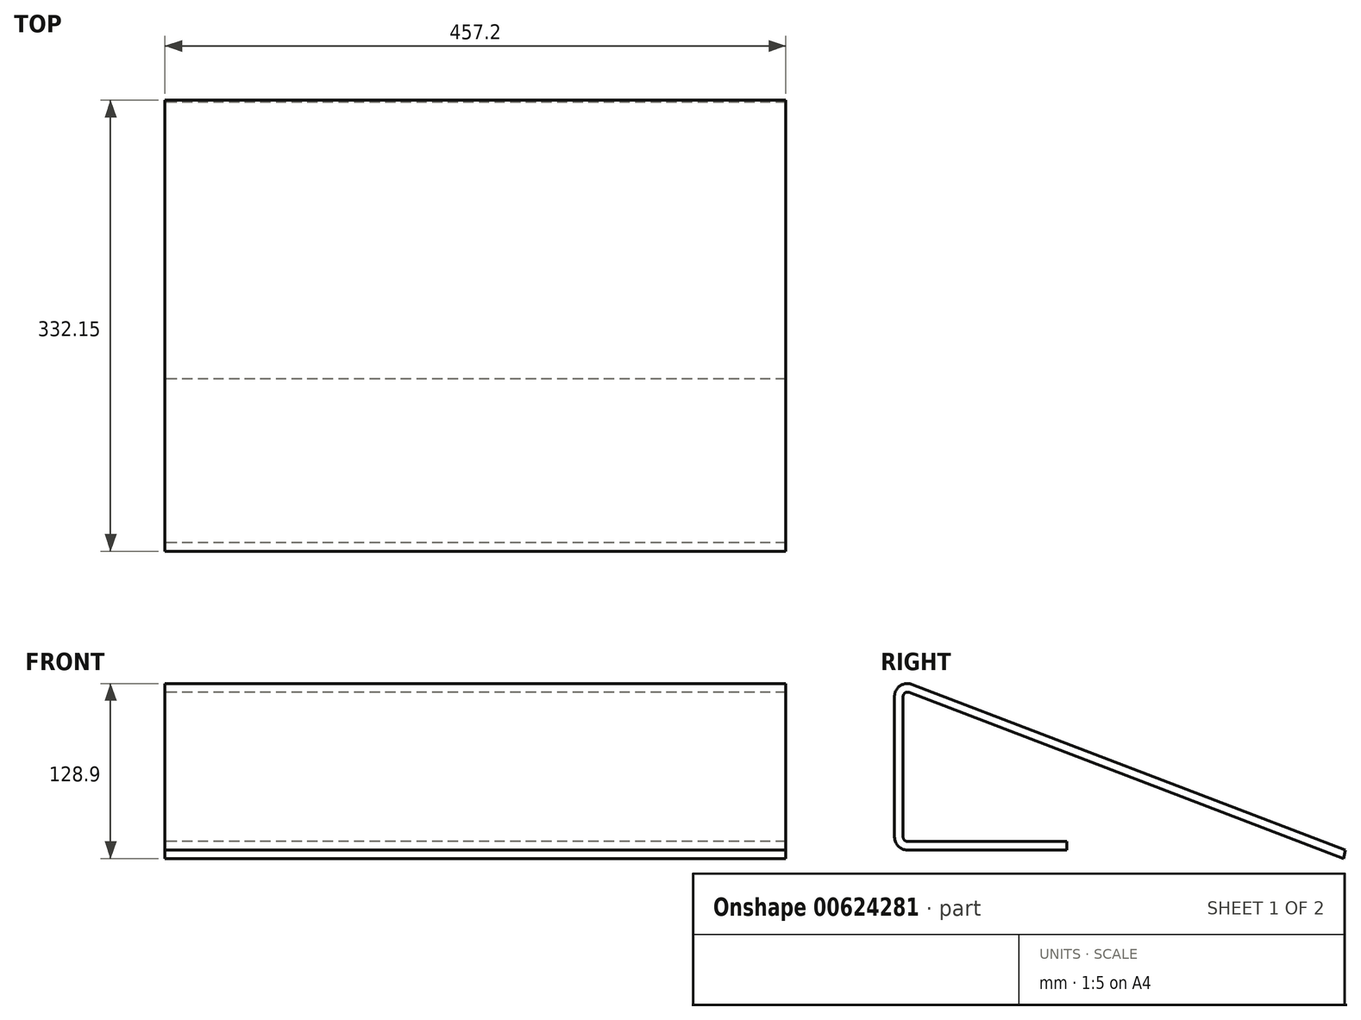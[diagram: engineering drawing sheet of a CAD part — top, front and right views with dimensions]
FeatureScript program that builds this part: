
annotation { "Feature Type Name" : "Feature", "Feature Type Description" : "" }
export const myFeature = defineFeature(function(context is Context, id is Id, definition is map)
    precondition{}
    {
        {
            var Q0;
            Q0=qCreatedBy(makeId("Right.planeOp"),FACE);
            var sketch = newSketch(context, id + "F0", { "sketchPlane" : qUnion([Q0])});
            skLineSegment(sketch, "E0", {"start": v(0, 0) * mm, "end": v(-117.47, 0) * mm});
            skLineSegment(sketch, "E1", {"start": v(-127, 9.52) * mm, "end": v(-127, 113.16) * mm});
            skLineSegment(sketch, "E2", {"start": v(-114.07, 122.06) * mm, "end": v(205.15, 0) * mm});
            skPoint(sketch, "E3.visualSharp", {"position": v(-127, 127) * mm});
            skArc(sketch, "E3.filletArc", {"start": v(-114.07, 122.06) * mm, "mid": v(-122.88, 121) * mm, "end": v(-127, 113.16) * mm});
            skPoint(sketch, "E4.visualSharp", {"position": v(-127, 0) * mm});
            skArc(sketch, "E4.filletArc", {"start": v(-127, 9.52) * mm, "mid": v(-124.21, 2.79) * mm, "end": v(-117.47, 0) * mm});
            skLineSegment(sketch, "E5", {"start": v(0, 0) * mm, "end": v(0, 6.35) * mm});
            skLineSegment(sketch, "E6", {"start": v(0, 6.35) * mm, "end": v(-117.48, 6.35) * mm});
            skLineSegment(sketch, "E7", {"start": v(-120.65, 9.52) * mm, "end": v(-120.65, 113.16) * mm});
            skLineSegment(sketch, "E8", {"start": v(-116.34, 116.13) * mm, "end": v(203.6, -6.2) * mm});
            skLineSegment(sketch, "E9", {"start": v(203.6, -6.2) * mm, "end": v(205.15, 0) * mm});
            skPoint(sketch, "E10.visualSharp", {"position": v(-120.65, 6.35) * mm});
            skArc(sketch, "E10.filletArc", {"start": v(-120.65, 9.52) * mm, "mid": v(-119.72, 7.28) * mm, "end": v(-117.48, 6.35) * mm});
            skPoint(sketch, "E11.visualSharp", {"position": v(-120.65, 117.77) * mm});
            skArc(sketch, "E11.filletArc", {"start": v(-116.34, 116.13) * mm, "mid": v(-119.28, 115.78) * mm, "end": v(-120.65, 113.16) * mm});
            skSolve(sketch);
        }
        {
            var Q0;
            Q0 = qSketchRegion(id + "F0", true);
            extrude(context, id + "F1", {"entities" : qUnion([Q0]), "depth" : 228.6 * mm, "offsetDistance" : 25.4 * mm, "hasSecondDirection" : true, "secondDirectionOppositeDirection" : true, "secondDirectionDepth" : 228.6 * mm});
        }
    });
